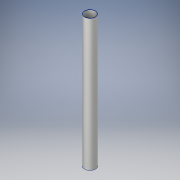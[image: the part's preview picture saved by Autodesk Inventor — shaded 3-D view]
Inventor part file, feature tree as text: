
AUTODESK INVENTOR PART (.ipt)
format: ipt  version: 2017 (Build 210142000, 142)  size: 94,720 bytes
history: native  units: in
note: dims shown in document units (in); Inventor stores cm internally (conversion verified against a paired STEP export)
features: extrude x1, sketch x1
ambient origin geometry x8: Origin, YZ Plane, XZ Plane, XY Plane, X Axis, Y Axis, Z Axis, Center Point
bodies: Solid1 (feature_tree)
feature tree (2):
  extrude  "Extrusion1"  Depth=24.0in
  sketch  "Sketch1"  dims[d0=2.0in d1=1.875in d2=24.0in d3=0.0in]
